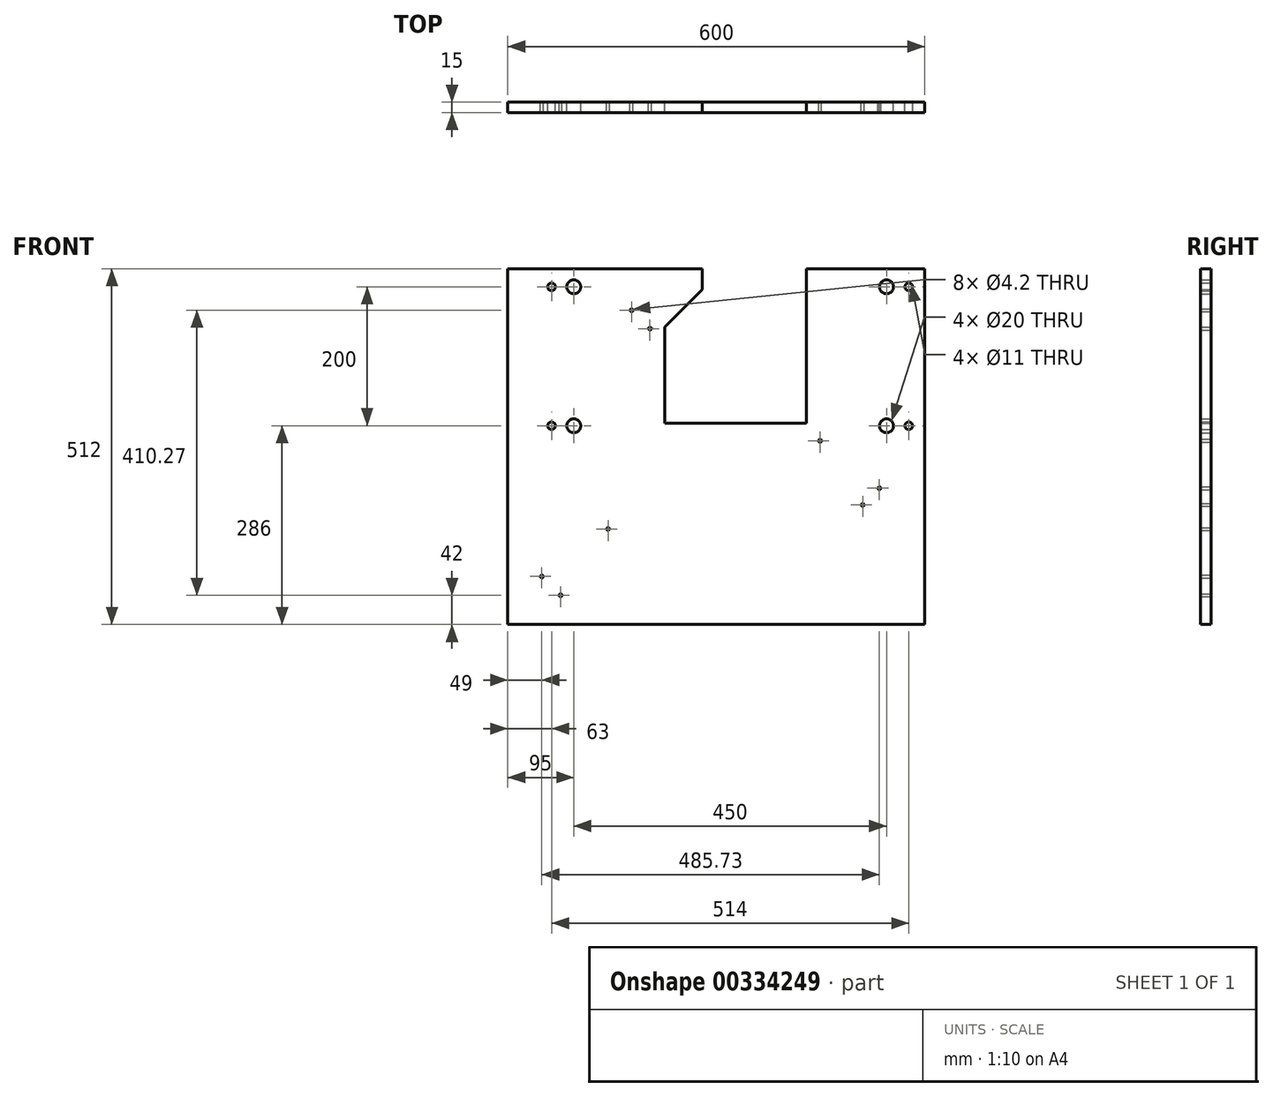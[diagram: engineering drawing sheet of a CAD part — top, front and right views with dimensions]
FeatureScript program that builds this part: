
annotation { "Feature Type Name" : "Feature", "Feature Type Description" : "" }
export const myFeature = defineFeature(function(context is Context, id is Id, definition is map)
    precondition{}
    {
        {
            var Q0;
            Q0=qCreatedBy(makeId("Front.planeOp"),FACE);
            var sketch = newSketch(context, id + "F0", { "sketchPlane" : qUnion([Q0])});
            skLineSegment(sketch, "E0.top", {"start": v(-300, -290) * mm, "end": v(300, -290) * mm});
            skLineSegment(sketch, "E0.left", {"start": v(-300, 222) * mm, "end": v(-300, -290) * mm});
            skLineSegment(sketch, "E0.right", {"start": v(300, 222) * mm, "end": v(300, -290) * mm});
            skLineSegment(sketch, "E1", {"start": v(0, 278.83) * mm, "end": v(0, -290) * mm, "construction": true});
            skPoint(sketch, "E2", {"position": v(0, 222) * mm});
            skLineSegment(sketch, "E3", {"start": v(-300, 222) * mm, "end": v(-20, 222) * mm});
            skLineSegment(sketch, "E4", {"start": v(-74, 0) * mm, "end": v(130, 0) * mm});
            skLineSegment(sketch, "E5", {"start": v(130, 0) * mm, "end": v(130, 222) * mm});
            skLineSegment(sketch, "E6", {"start": v(130, 222) * mm, "end": v(300, 222) * mm});
            skLineSegment(sketch, "E7", {"start": v(-20, 222) * mm, "end": v(-20, 192) * mm});
            skLineSegment(sketch, "E8", {"start": v(-20, 192) * mm, "end": v(-74, 138) * mm});
            skLineSegment(sketch, "E9", {"start": v(-74, 138) * mm, "end": v(-74, 0) * mm});
            skSolve(sketch);
        }
        {
            var Q0;
            Q0=makeQuery(id+"F0.imprint","IMPRINT",FACE,{"disambiguationData":[TD([[makeQuery(id+"F0.imprint","IMPRINT",EDGE,{"derivedFrom":sQuery(id+"F0.wireOp",EDGE,"E0.top")}),1.0]])]});
            extrude(context, id + "F1", {"entities" : qUnion([Q0]), "endBound" : BoundingType.SYMMETRIC, "depth" : 15 * mm});
        }
        {
            var Q0;
            Q0=makeQuery(id+"F1.opExtrude","CAP_FACE",FACE,{"disambiguationData":[OSD([sQuery(id+"F0.wireOp",EDGE,"E0.top"),sQuery(id+"F0.wireOp",EDGE,"E0.left"),sQuery(id+"F0.wireOp",EDGE,"E0.right"),sQuery(id+"F0.wireOp",EDGE,"E3"),sQuery(id+"F0.wireOp",EDGE,"E4"),sQuery(id+"F0.wireOp",EDGE,"E5"),sQuery(id+"F0.wireOp",EDGE,"E6"),sQuery(id+"F0.wireOp",EDGE,"E7"),sQuery(id+"F0.wireOp",EDGE,"E8"),sQuery(id+"F0.wireOp",EDGE,"E9")])],"isStart":true});
            var sketch = newSketch(context, id + "F2", { "sketchPlane" : qUnion([Q0])});
            skLineSegment(sketch, "E10.bottom", {"start": v(-245, 196) * mm, "end": v(205, 196) * mm, "construction": true});
            skLineSegment(sketch, "E10.top", {"start": v(-245, -4) * mm, "end": v(205, -4) * mm, "construction": true});
            skLineSegment(sketch, "E10.left", {"start": v(-245, 196) * mm, "end": v(-245, -4) * mm, "construction": true});
            skLineSegment(sketch, "E10.right", {"start": v(205, 196) * mm, "end": v(205, -4) * mm, "construction": true});
            skSolve(sketch);
        }
        {
            var Q0;
            Q0=sQuery(id+"F2.wireOp",VERTEX,"E10.left.start");
            var Q1;
            Q1=sQuery(id+"F2.wireOp",VERTEX,"E10.right.start");
            var Q2;
            Q2=sQuery(id+"F2.wireOp",VERTEX,"E10.left.end");
            var Q3;
            Q3=sQuery(id+"F2.wireOp",VERTEX,"E10.top.end");
            var Q4;
            Q4=makeQuery(id+"F1.opExtrude","SWEPT_BODY",BODY,{"disambiguationData":[OSD([sQuery(id+"F0.wireOp",EDGE,"E0.top"),sQuery(id+"F0.wireOp",EDGE,"E0.left"),sQuery(id+"F0.wireOp",EDGE,"E0.right"),sQuery(id+"F0.wireOp",EDGE,"E3"),sQuery(id+"F0.wireOp",EDGE,"E4"),sQuery(id+"F0.wireOp",EDGE,"E5"),sQuery(id+"F0.wireOp",EDGE,"E6"),sQuery(id+"F0.wireOp",EDGE,"E7"),sQuery(id+"F0.wireOp",EDGE,"E8"),sQuery(id+"F0.wireOp",EDGE,"E9")])]});
            hole(context, id + "F3", {"style" : HoleStyle.SIMPLE, "endStyle" : HoleEndStyle.THROUGH, "standardTappedOrClearance" : lookupTablePath({ "standard" : "ISO", "size" : "20", "type" : "Drilled" }), "standardBlindInLast" : lookupTablePath({ "standard" : "ISO", "size" : "20", "type" : "Drilled" }), "holeDiameter" : 20 * mm, "tappedDepth" : 12 * mm, "tapClearance" : 3, "locations" : qUnion([Q0, Q1, Q2, Q3]), "scope" : qUnion([Q4])});
        }
        {
            var Q0;
            Q0=makeQuery(id+"F1.opExtrude","CAP_FACE",FACE,{"disambiguationData":[OSD([sQuery(id+"F0.wireOp",EDGE,"E0.top"),sQuery(id+"F0.wireOp",EDGE,"E0.left"),sQuery(id+"F0.wireOp",EDGE,"E0.right"),sQuery(id+"F0.wireOp",EDGE,"E3"),sQuery(id+"F0.wireOp",EDGE,"E4"),sQuery(id+"F0.wireOp",EDGE,"E5"),sQuery(id+"F0.wireOp",EDGE,"E6"),sQuery(id+"F0.wireOp",EDGE,"E7"),sQuery(id+"F0.wireOp",EDGE,"E8"),sQuery(id+"F0.wireOp",EDGE,"E9")])],"isStart":true});
            var sketch = newSketch(context, id + "F4", { "sketchPlane" : qUnion([Q0])});
            skPoint(sketch, "E11", {"position": v(-234.73, -93.85) * mm});
            skPoint(sketch, "E12", {"position": v(-210.69, -117.89) * mm});
            skPoint(sketch, "E13", {"position": v(-149.39, -25.55) * mm});
            skPoint(sketch, "E14", {"position": v(223.96, -248) * mm});
            skPoint(sketch, "E15", {"position": v(251, -220.96) * mm});
            skPoint(sketch, "E16", {"position": v(155.66, -152.66) * mm});
            skLineSegment(sketch, "E17", {"start": v(-234.73, -93.85) * mm, "end": v(-210.69, -117.89) * mm, "construction": true});
            skLineSegment(sketch, "E18", {"start": v(-149.39, -25.55) * mm, "end": v(-210.69, -117.9) * mm, "construction": true});
            skLineSegment(sketch, "E19", {"start": v(-234.73, -93.85) * mm, "end": v(-149.39, -25.55) * mm, "construction": true});
            skPoint(sketch, "E20", {"position": v(95.42, 135.79) * mm});
            skPoint(sketch, "E21", {"position": v(121.9, 162.27) * mm});
            skSolve(sketch);
        }
        {
            var Q0;
            Q0=sQuery(id+"F4.wireOp",VERTEX,"E12");
            var Q1;
            Q1=sQuery(id+"F4.wireOp",VERTEX,"E11");
            var Q2;
            Q2=sQuery(id+"F4.wireOp",VERTEX,"E13");
            var Q3;
            Q3=sQuery(id+"F4.wireOp",VERTEX,"E16");
            var Q4;
            Q4=sQuery(id+"F4.wireOp",VERTEX,"E14");
            var Q5;
            Q5=sQuery(id+"F4.wireOp",VERTEX,"E15");
            var Q6;
            Q6=sQuery(id+"F4.wireOp",VERTEX,"E20");
            var Q7;
            Q7=sQuery(id+"F4.wireOp",VERTEX,"E21");
            var Q8;
            Q8=makeQuery(id+"F1.opExtrude","SWEPT_BODY",BODY,{"disambiguationData":[OSD([sQuery(id+"F0.wireOp",EDGE,"E0.top"),sQuery(id+"F0.wireOp",EDGE,"E0.left"),sQuery(id+"F0.wireOp",EDGE,"E0.right"),sQuery(id+"F0.wireOp",EDGE,"E3"),sQuery(id+"F0.wireOp",EDGE,"E4"),sQuery(id+"F0.wireOp",EDGE,"E5"),sQuery(id+"F0.wireOp",EDGE,"E6"),sQuery(id+"F0.wireOp",EDGE,"E7"),sQuery(id+"F0.wireOp",EDGE,"E8"),sQuery(id+"F0.wireOp",EDGE,"E9")])]});
            hole(context, id + "F5", {"style" : HoleStyle.SIMPLE, "endStyle" : HoleEndStyle.THROUGH, "standardTappedOrClearance" : lookupTablePath({ "standard" : "ISO", "engagement" : "75%", "pitch" : "0.8 mm", "size" : "M5", "type" : "Tapped" }), "standardBlindInLast" : lookupTablePath({ "standard" : "ISO", "engagement" : "75%", "pitch" : "0.8 mm", "size" : "M5", "type" : "Tapped" }), "holeDiameter" : 4.2 * mm, "showTappedDepth" : true, "tappedDepth" : 12 * mm, "tapClearance" : 3, "locations" : qUnion([Q0, Q1, Q2, Q3, Q4, Q5, Q6, Q7]), "scope" : qUnion([Q8]), "majorDiameter" : 5 * mm});
        }
        {
            var Q0;
            Q0=makeQuery(id+"F1.opExtrude","CAP_FACE",FACE,{"disambiguationData":[OSD([sQuery(id+"F0.wireOp",EDGE,"E0.top"),sQuery(id+"F0.wireOp",EDGE,"E0.left"),sQuery(id+"F0.wireOp",EDGE,"E0.right"),sQuery(id+"F0.wireOp",EDGE,"E3"),sQuery(id+"F0.wireOp",EDGE,"E4"),sQuery(id+"F0.wireOp",EDGE,"E5"),sQuery(id+"F0.wireOp",EDGE,"E6"),sQuery(id+"F0.wireOp",EDGE,"E7"),sQuery(id+"F0.wireOp",EDGE,"E8"),sQuery(id+"F0.wireOp",EDGE,"E9")])],"isStart":true});
            var sketch = newSketch(context, id + "F6", { "sketchPlane" : qUnion([Q0])});
            skLineSegment(sketch, "E22.bottom", {"start": v(-277, 196) * mm, "end": v(237, 196) * mm, "construction": true});
            skLineSegment(sketch, "E22.top", {"start": v(-277, -4) * mm, "end": v(237, -4) * mm, "construction": true});
            skLineSegment(sketch, "E22.left", {"start": v(-277, 196) * mm, "end": v(-277, -4) * mm, "construction": true});
            skLineSegment(sketch, "E22.right", {"start": v(237, 196) * mm, "end": v(237, -4) * mm, "construction": true});
            skPoint(sketch, "E23", {"position": v(-245, -4) * mm});
            skPoint(sketch, "E24", {"position": v(-245, 196) * mm});
            skPoint(sketch, "E25", {"position": v(205, 196) * mm});
            skPoint(sketch, "E26", {"position": v(205, -4) * mm});
            skSolve(sketch);
        }
        {
            var Q0;
            Q0=sQuery(id+"F6.wireOp",VERTEX,"E22.left.start");
            var Q1;
            Q1=sQuery(id+"F6.wireOp",VERTEX,"E22.left.end");
            var Q2;
            Q2=sQuery(id+"F6.wireOp",VERTEX,"E22.right.start");
            var Q3;
            Q3=sQuery(id+"F6.wireOp",VERTEX,"E22.right.end");
            var Q4;
            Q4=makeQuery(id+"F1.opExtrude","SWEPT_BODY",BODY,{"disambiguationData":[OSD([sQuery(id+"F0.wireOp",EDGE,"E0.top"),sQuery(id+"F0.wireOp",EDGE,"E0.left"),sQuery(id+"F0.wireOp",EDGE,"E0.right"),sQuery(id+"F0.wireOp",EDGE,"E3"),sQuery(id+"F0.wireOp",EDGE,"E4"),sQuery(id+"F0.wireOp",EDGE,"E5"),sQuery(id+"F0.wireOp",EDGE,"E6"),sQuery(id+"F0.wireOp",EDGE,"E7"),sQuery(id+"F0.wireOp",EDGE,"E8"),sQuery(id+"F0.wireOp",EDGE,"E9")])]});
            hole(context, id + "F7", {"style" : HoleStyle.SIMPLE, "endStyle" : HoleEndStyle.THROUGH, "standardTappedOrClearance" : lookupTablePath({ "standard" : "ISO", "fit" : "Normal", "size" : "M10", "type" : "Clearance" }), "standardBlindInLast" : lookupTablePath({ "fit" : "Standard", "standard" : "ISO", "size" : "M10", "type" : "Clearance" }), "holeDiameter" : 11 * mm, "tappedDepth" : 6.75 * mm, "tapClearance" : 3, "locations" : qUnion([Q0, Q1, Q2, Q3]), "scope" : qUnion([Q4])});
        }
    });
